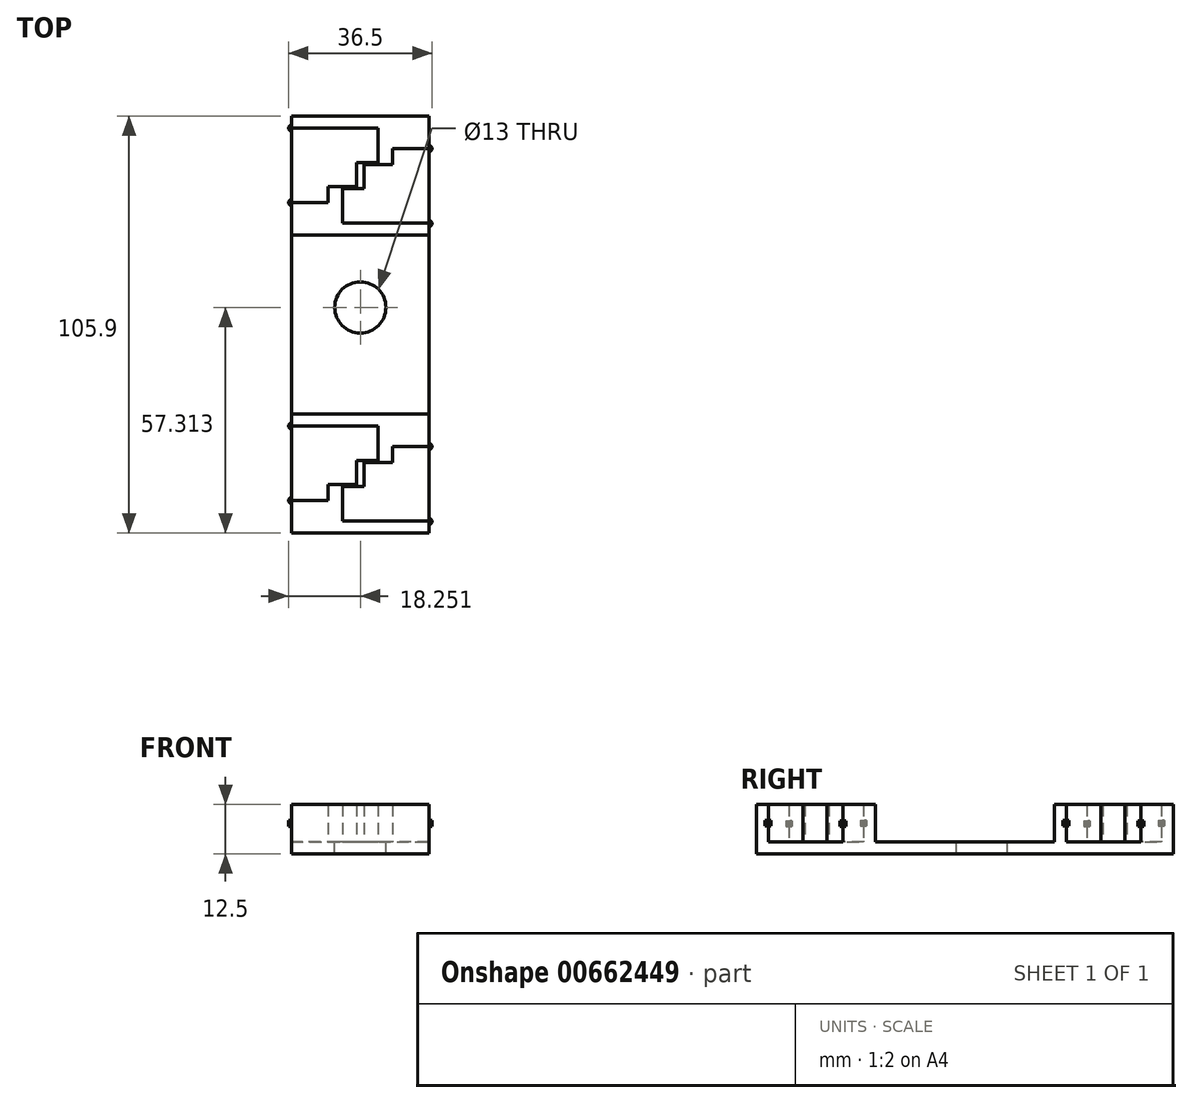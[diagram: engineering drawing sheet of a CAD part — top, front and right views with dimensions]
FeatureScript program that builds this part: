
annotation { "Feature Type Name" : "Feature", "Feature Type Description" : "" }
export const myFeature = defineFeature(function(context is Context, id is Id, definition is map)
    precondition{}
    {
        {
            var Q0;
            Q0=qCreatedBy(makeId("Top.planeOp"),FACE);
            var sketch = newSketch(context, id + "F0", { "sketchPlane" : qUnion([Q0])});
            skLineSegment(sketch, "E0.bottom", {"start": v(-9.64, 16.1) * mm, "end": v(7.86, 16.1) * mm});
            skLineSegment(sketch, "E0.left", {"start": v(-9.64, 16.1) * mm, "end": v(-9.64, -29.4) * mm});
            skLineSegment(sketch, "E1", {"start": v(7.86, 16.1) * mm, "end": v(25.36, 16.1) * mm});
            skCircle(sketch, "E2", {"center": v(7.86, -2.29) * mm, "radius": 6.5 * mm});
            skLineSegment(sketch, "E3.MirrorCS", {"start": v(-9.64, 43.3) * mm, "end": v(-6.47, 43.3) * mm});
            skLineSegment(sketch, "E4.MirrorCS", {"start": v(7.86, 27.9) * mm, "end": v(7.86, 34.5) * mm});
            skLineSegment(sketch, "E5.MirrorCS", {"start": v(-9.64, 24.3) * mm, "end": v(-0.34, 24.3) * mm});
            skLineSegment(sketch, "E6.MirrorCS", {"start": v(12.36, 35.3) * mm, "end": v(12.36, 43.3) * mm});
            skLineSegment(sketch, "E7.MirrorCS", {"start": v(-6.47, 43.3) * mm, "end": v(12.36, 43.3) * mm});
            skLineSegment(sketch, "E8.MirrorCS", {"start": v(-9.64, 24.3) * mm, "end": v(-9.64, 43.3) * mm});
            skPoint(sketch, "E9", {"position": v(7.86, 31.6) * mm});
            skLineSegment(sketch, "E10", {"start": v(-9.64, 16.1) * mm, "end": v(-9.64, 19.1) * mm});
            skLineSegment(sketch, "E11", {"start": v(-9.64, 19.1) * mm, "end": v(25.36, 19.1) * mm});
            skLineSegment(sketch, "E12", {"start": v(25.36, 19.1) * mm, "end": v(25.36, 19.1) * mm});
            skLineSegment(sketch, "E13", {"start": v(25.36, 19.1) * mm, "end": v(25.36, 16.1) * mm});
            skLineSegment(sketch, "E14.MirrorCS", {"start": v(25.36, 19.1) * mm, "end": v(22.2, 19.1) * mm});
            skLineSegment(sketch, "E15.MirrorCS", {"start": v(7.86, 34.5) * mm, "end": v(7.86, 27.9) * mm});
            skLineSegment(sketch, "E16.MirrorCS", {"start": v(25.36, 38.1) * mm, "end": v(16.06, 38.1) * mm});
            skLineSegment(sketch, "E17.MirrorCS", {"start": v(3.36, 27.1) * mm, "end": v(3.36, 19.1) * mm});
            skLineSegment(sketch, "E18.MirrorCS", {"start": v(22.2, 19.1) * mm, "end": v(3.36, 19.1) * mm});
            skLineSegment(sketch, "E19.MirrorCS", {"start": v(25.36, 38.1) * mm, "end": v(25.36, 19.1) * mm});
            skPoint(sketch, "E20", {"position": v(7.86, 30.8) * mm});
            skLineSegment(sketch, "E21", {"start": v(-9.64, 19.1) * mm, "end": v(-9.64, 24.3) * mm});
            skLineSegment(sketch, "E22", {"start": v(12.36, 43.3) * mm, "end": v(25.36, 43.3) * mm});
            skLineSegment(sketch, "E23", {"start": v(25.36, 43.3) * mm, "end": v(25.36, 38.1) * mm});
            skLineSegment(sketch, "E24", {"start": v(-9.64, 43.3) * mm, "end": v(-9.64, 46.3) * mm});
            skLineSegment(sketch, "E25", {"start": v(-9.64, 46.3) * mm, "end": v(25.36, 46.3) * mm});
            skLineSegment(sketch, "E26", {"start": v(25.36, 46.3) * mm, "end": v(25.36, 43.3) * mm});
            skLineSegment(sketch, "E27", {"start": v(25.36, -29.4) * mm, "end": v(-9.64, -29.4) * mm});
            skLineSegment(sketch, "E28", {"start": v(16.06, 38.1) * mm, "end": v(16.06, 34) * mm});
            skLineSegment(sketch, "E29", {"start": v(16.06, 34) * mm, "end": v(7.86, 34) * mm});
            skLineSegment(sketch, "E30", {"start": v(7.86, 34.5) * mm, "end": v(12.36, 34.5) * mm});
            skLineSegment(sketch, "E31", {"start": v(12.36, 34.5) * mm, "end": v(12.36, 35.3) * mm});
            skLineSegment(sketch, "E32", {"start": v(-0.34, 24.3) * mm, "end": v(-0.34, 28.4) * mm});
            skLineSegment(sketch, "E33", {"start": v(7.86, 27.9) * mm, "end": v(3.36, 27.9) * mm});
            skLineSegment(sketch, "E34", {"start": v(3.36, 27.9) * mm, "end": v(3.36, 27.1) * mm});
            skLineSegment(sketch, "E35", {"start": v(7.86, 34.5) * mm, "end": v(6.93, 34.5) * mm});
            skLineSegment(sketch, "E36", {"start": v(7.86, 27.9) * mm, "end": v(8.8, 27.9) * mm});
            skLineSegment(sketch, "E37", {"start": v(6.93, 34.5) * mm, "end": v(6.93, 28.4) * mm});
            skLineSegment(sketch, "E38", {"start": v(8.8, 27.9) * mm, "end": v(8.8, 34) * mm});
            skLineSegment(sketch, "E39", {"start": v(-0.34, 28.4) * mm, "end": v(7.86, 28.4) * mm});
            skPoint(sketch, "E40", {"position": v(-9.64, -6.65) * mm});
            skLineSegment(sketch, "E41", {"start": v(-37.32, -6.65) * mm, "end": v(44.88, -6.65) * mm, "construction": true});
            skLineSegment(sketch, "E42", {"start": v(25.36, 16.1) * mm, "end": v(25.36, -29.4) * mm});
            skLineSegment(sketch, "E43.MirrorCS", {"start": v(-9.64, -32.4) * mm, "end": v(-6.47, -32.4) * mm});
            skLineSegment(sketch, "E44.MirrorCS", {"start": v(7.86, -47.8) * mm, "end": v(7.86, -41.2) * mm});
            skLineSegment(sketch, "E45.MirrorCS", {"start": v(-9.64, -51.4) * mm, "end": v(-0.34, -51.4) * mm});
            skLineSegment(sketch, "E46.MirrorCS", {"start": v(12.36, -40.4) * mm, "end": v(12.36, -32.4) * mm});
            skLineSegment(sketch, "E47.MirrorCS", {"start": v(-6.47, -32.4) * mm, "end": v(12.36, -32.4) * mm});
            skLineSegment(sketch, "E48.MirrorCS", {"start": v(-9.64, -51.4) * mm, "end": v(-9.64, -32.4) * mm});
            skPoint(sketch, "E49", {"position": v(7.86, -44.1) * mm});
            skLineSegment(sketch, "E50", {"start": v(-9.64, -56.6) * mm, "end": v(25.36, -56.6) * mm});
            skLineSegment(sketch, "E51", {"start": v(21.02, 47.75) * mm, "end": v(21.02, 47.75) * mm});
            skLineSegment(sketch, "E52.MirrorCS", {"start": v(25.36, -56.6) * mm, "end": v(22.2, -56.6) * mm});
            skLineSegment(sketch, "E53.MirrorCS", {"start": v(7.86, -41.2) * mm, "end": v(7.86, -47.8) * mm});
            skLineSegment(sketch, "E54.MirrorCS", {"start": v(25.36, -37.6) * mm, "end": v(16.06, -37.6) * mm});
            skLineSegment(sketch, "E55.MirrorCS", {"start": v(3.36, -48.6) * mm, "end": v(3.36, -56.6) * mm});
            skLineSegment(sketch, "E56.MirrorCS", {"start": v(22.2, -56.6) * mm, "end": v(3.36, -56.6) * mm});
            skLineSegment(sketch, "E57.MirrorCS", {"start": v(25.36, -37.6) * mm, "end": v(25.36, -56.6) * mm});
            skPoint(sketch, "E58", {"position": v(7.86, -44.9) * mm});
            skLineSegment(sketch, "E59", {"start": v(-9.64, -56.6) * mm, "end": v(-9.64, -51.4) * mm});
            skLineSegment(sketch, "E60", {"start": v(12.36, -32.4) * mm, "end": v(25.36, -32.4) * mm});
            skLineSegment(sketch, "E61", {"start": v(25.36, -32.4) * mm, "end": v(25.36, -37.6) * mm});
            skLineSegment(sketch, "E62", {"start": v(-9.64, -32.4) * mm, "end": v(-9.64, -29.4) * mm});
            skLineSegment(sketch, "E63", {"start": v(-9.64, -29.4) * mm, "end": v(25.36, -29.4) * mm});
            skLineSegment(sketch, "E64", {"start": v(25.36, -29.4) * mm, "end": v(25.36, -32.4) * mm});
            skLineSegment(sketch, "E65", {"start": v(16.06, -37.6) * mm, "end": v(16.06, -41.7) * mm});
            skLineSegment(sketch, "E66", {"start": v(16.06, -41.7) * mm, "end": v(7.86, -41.7) * mm});
            skLineSegment(sketch, "E67", {"start": v(7.86, -41.2) * mm, "end": v(12.36, -41.2) * mm});
            skLineSegment(sketch, "E68", {"start": v(12.36, -41.2) * mm, "end": v(12.36, -40.4) * mm});
            skLineSegment(sketch, "E69", {"start": v(-0.34, -51.4) * mm, "end": v(-0.34, -47.3) * mm});
            skLineSegment(sketch, "E70", {"start": v(7.86, -47.8) * mm, "end": v(3.36, -47.8) * mm});
            skLineSegment(sketch, "E71", {"start": v(3.36, -47.8) * mm, "end": v(3.36, -48.6) * mm});
            skLineSegment(sketch, "E72", {"start": v(7.86, -41.2) * mm, "end": v(6.93, -41.2) * mm});
            skLineSegment(sketch, "E73", {"start": v(7.86, -47.8) * mm, "end": v(8.8, -47.8) * mm});
            skLineSegment(sketch, "E74", {"start": v(6.93, -41.2) * mm, "end": v(6.93, -47.3) * mm});
            skLineSegment(sketch, "E75", {"start": v(8.8, -47.8) * mm, "end": v(8.8, -41.7) * mm});
            skLineSegment(sketch, "E76", {"start": v(-0.34, -47.3) * mm, "end": v(7.86, -47.3) * mm});
            skLineSegment(sketch, "E77", {"start": v(-9.64, -59.6) * mm, "end": v(-9.64, -56.6) * mm});
            skLineSegment(sketch, "E78", {"start": v(-9.64, -59.6) * mm, "end": v(25.36, -59.6) * mm});
            skLineSegment(sketch, "E79", {"start": v(25.36, -59.6) * mm, "end": v(25.36, -56.6) * mm});
            skSolve(sketch);
        }
        {
            var Q0;
            Q0=makeQuery(id+"F0.imprint","IMPRINT",FACE,{"disambiguationData":[TD([[makeQuery(id+"F0.imprint","IMPRINT",EDGE,{"derivedFrom":sQuery(id+"F0.wireOp",EDGE,"E0.bottom")}),-1.0]])]});
            var Q1;
            Q1=makeQuery(id+"F0.imprint","IMPRINT",FACE,{"disambiguationData":[TD([[makeQuery(id+"F0.imprint","IMPRINT",EDGE,{"derivedFrom":sQuery(id+"F0.wireOp",EDGE,"E27")}),1.0]])]});
            var Q2;
            Q2=makeQuery(id+"F0.imprint","IMPRINT",FACE,{"disambiguationData":[TD([[makeQuery(id+"F0.imprint","IMPRINT",EDGE,{"derivedFrom":sQuery(id+"F0.wireOp",EDGE,"82a180c3-1ea1-40ab-986d-dace1a723f1b2.MirrorCS")}),1.0]])]});
            var Q3;
            Q3=makeQuery(id+"F0.imprint","IMPRINT",FACE,{"disambiguationData":[TD([[makeQuery(id+"F0.imprint","IMPRINT",EDGE,{"derivedFrom":sQuery(id+"F0.wireOp",EDGE,"82a180c3-1ea1-40ab-986d-dace1a723f1b1.MirrorCS")}),1.0]])]});
            var Q4;
            Q4=makeQuery(id+"F0.imprint","IMPRINT",FACE,{"disambiguationData":[TD([[makeQuery(id+"F0.imprint","IMPRINT",EDGE,{"derivedFrom":sQuery(id+"F0.wireOp",EDGE,"82a180c3-1ea1-40ab-986d-dace1a723f1b4.MirrorCS")}),1.0]])]});
            var Q5;
            {var subQ2=sQuery(id+"F0.wireOp",EDGE,"82a180c3-1ea1-40ab-986d-dace1a723f1b0.MirrorCS");Q5=makeQuery(id+"F0.imprint","IMPRINT",FACE,{"disambiguationData":[TD([[makeQuery(id+"F0.imprint","IMPRINT",EDGE,{"derivedFrom":subQ2}),-1.0]])]});}
            var Q6;
            {var subQ5=sQuery(id+"F0.wireOp",EDGE,"82a180c3-1ea1-40ab-986d-dace1a723f1b1.MirrorCS");Q6=makeQuery(id+"F0.imprint","IMPRINT",FACE,{"disambiguationData":[TD([[makeQuery(id+"F0.imprint","IMPRINT",EDGE,{"derivedFrom":subQ5}),-1.0]])]});}
            var Q7;
            Q7=makeQuery(id+"F0.imprint","IMPRINT",FACE,{"disambiguationData":[TD([[makeQuery(id+"F0.imprint","IMPRINT",EDGE,{"derivedFrom":sQuery(id+"F0.wireOp",EDGE,"82a180c3-1ea1-40ab-986d-dace1a723f1b0.MirrorCS")}),1.0]])]});
            var Q8;
            Q8=makeQuery(id+"F0.imprint","IMPRINT",FACE,{"disambiguationData":[TD([[makeQuery(id+"F0.imprint","IMPRINT",EDGE,{"derivedFrom":sQuery(id+"F0.wireOp",EDGE,"82a180c3-1ea1-40ab-986d-dace1a723f1b16.MirrorCS")}),-1.0]])]});
            var Q9;
            Q9=makeQuery(id+"F0.imprint","IMPRINT",FACE,{"disambiguationData":[TD([[makeQuery(id+"F0.imprint","IMPRINT",EDGE,{"derivedFrom":sQuery(id+"F0.wireOp",EDGE,"E3.MirrorCS")}),1.0]])]});
            var Q10;
            Q10=makeQuery(id+"F0.imprint","IMPRINT",FACE,{"disambiguationData":[TD([[makeQuery(id+"F0.imprint","IMPRINT",EDGE,{"derivedFrom":sQuery(id+"F0.wireOp",EDGE,"E6.MirrorCS")}),-1.0]])]});
            var Q11;
            Q11=makeQuery(id+"F0.imprint","IMPRINT",FACE,{"disambiguationData":[TD([[makeQuery(id+"F0.imprint","IMPRINT",EDGE,{"derivedFrom":sQuery(id+"F0.wireOp",EDGE,"E3.MirrorCS")}),-1.0]])]});
            var Q12;
            Q12=makeQuery(id+"F0.imprint","IMPRINT",FACE,{"disambiguationData":[TD([[makeQuery(id+"F0.imprint","IMPRINT",EDGE,{"derivedFrom":sQuery(id+"F0.wireOp",EDGE,"E16.MirrorCS")}),1.0]])]});
            var Q13;
            Q13=makeQuery(id+"F0.imprint","IMPRINT",FACE,{"disambiguationData":[TD([[makeQuery(id+"F0.imprint","IMPRINT",EDGE,{"derivedFrom":sQuery(id+"F0.wireOp",EDGE,"E0.bottom")}),1.0]])]});
            var Q14;
            Q14=makeQuery(id+"F0.imprint","IMPRINT",FACE,{"disambiguationData":[TD([[makeQuery(id+"F0.imprint","IMPRINT",EDGE,{"derivedFrom":sQuery(id+"F0.wireOp",EDGE,"E5.MirrorCS")}),-1.0]])]});
            var Q15;
            {var subQ1=sQuery(id+"F0.wireOp",EDGE,"E35");Q15=makeQuery(id+"F0.imprint","IMPRINT",FACE,{"disambiguationData":[TD([[makeQuery(id+"F0.imprint","IMPRINT",EDGE,{"derivedFrom":subQ1}),1.0]])]});}
            var Q16;
            {var subQ4=sQuery(id+"F0.wireOp",EDGE,"E36");Q16=makeQuery(id+"F0.imprint","IMPRINT",FACE,{"disambiguationData":[TD([[makeQuery(id+"F0.imprint","IMPRINT",EDGE,{"derivedFrom":subQ4}),1.0]])]});}
            var Q17;
            Q17=makeQuery(id+"F0.imprint","IMPRINT",FACE,{"disambiguationData":[TD([[makeQuery(id+"F0.imprint","IMPRINT",EDGE,{"derivedFrom":sQuery(id+"F0.wireOp",EDGE,"E43.MirrorCS")}),-1.0]])]});
            var Q18;
            Q18=makeQuery(id+"F0.imprint","IMPRINT",FACE,{"disambiguationData":[TD([[makeQuery(id+"F0.imprint","IMPRINT",EDGE,{"derivedFrom":sQuery(id+"F0.wireOp",EDGE,"E54.MirrorCS")}),1.0]])]});
            var Q19;
            Q19=makeQuery(id+"F0.imprint","IMPRINT",FACE,{"disambiguationData":[TD([[makeQuery(id+"F0.imprint","IMPRINT",EDGE,{"derivedFrom":sQuery(id+"F0.wireOp",EDGE,"E46.MirrorCS")}),-1.0]])]});
            var Q20;
            Q20=makeQuery(id+"F0.imprint","IMPRINT",FACE,{"disambiguationData":[TD([[makeQuery(id+"F0.imprint","IMPRINT",EDGE,{"derivedFrom":sQuery(id+"F0.wireOp",EDGE,"E27")}),1.0]])]});
            var Q21;
            Q21=makeQuery(id+"F0.imprint","IMPRINT",FACE,{"disambiguationData":[TD([[makeQuery(id+"F0.imprint","IMPRINT",EDGE,{"derivedFrom":sQuery(id+"F0.wireOp",EDGE,"E45.MirrorCS")}),-1.0]])]});
            var Q22;
            {var subQ0=sQuery(id+"F0.wireOp",EDGE,"E73");Q22=makeQuery(id+"F0.imprint","IMPRINT",FACE,{"disambiguationData":[TD([[makeQuery(id+"F0.imprint","IMPRINT",EDGE,{"derivedFrom":subQ0}),1.0]])]});}
            var Q23;
            {var subQ1=sQuery(id+"F0.wireOp",EDGE,"E72");Q23=makeQuery(id+"F0.imprint","IMPRINT",FACE,{"disambiguationData":[TD([[makeQuery(id+"F0.imprint","IMPRINT",EDGE,{"derivedFrom":subQ1}),1.0]])]});}
            var Q24;
            {var subQ4=sQuery(id+"F0.wireOp",EDGE,"E77");Q24=makeQuery(id+"F0.imprint","IMPRINT",FACE,{"disambiguationData":[TD([[makeQuery(id+"F0.imprint","IMPRINT",EDGE,{"derivedFrom":subQ4}),-1.0]])]});}
            extrude(context, id + "F1", {"entities" : qUnion([Q0, Q1, Q2, Q3, Q4, Q5, Q6, Q7, Q8, Q9, Q10, Q11, Q12, Q13, Q14, Q15, Q16, Q17, Q18, Q19, Q20, Q21, Q22, Q23, Q24]), "oppositeDirection" : true, "depth" : 3 * mm, "offsetDistance" : 25 * mm});
        }
        {
            var Q0;
            Q0=makeQuery(id+"F0.imprint","IMPRINT",FACE,{"disambiguationData":[TD([[makeQuery(id+"F0.imprint","IMPRINT",EDGE,{"derivedFrom":sQuery(id+"F0.wireOp",EDGE,"E0.bottom")}),1.0]])]});
            var Q1;
            Q1=makeQuery(id+"F0.imprint","IMPRINT",FACE,{"disambiguationData":[TD([[makeQuery(id+"F0.imprint","IMPRINT",EDGE,{"derivedFrom":sQuery(id+"F0.wireOp",EDGE,"E5.MirrorCS")}),-1.0]])]});
            var Q2;
            Q2=makeQuery(id+"F0.imprint","IMPRINT",FACE,{"disambiguationData":[TD([[makeQuery(id+"F0.imprint","IMPRINT",EDGE,{"derivedFrom":sQuery(id+"F0.wireOp",EDGE,"E3.MirrorCS")}),1.0]])]});
            var Q3;
            Q3=makeQuery(id+"F0.imprint","IMPRINT",FACE,{"disambiguationData":[TD([[makeQuery(id+"F0.imprint","IMPRINT",EDGE,{"derivedFrom":sQuery(id+"F0.wireOp",EDGE,"E6.MirrorCS")}),-1.0]])]});
            var Q4;
            {var subQ1=sQuery(id+"F0.wireOp",EDGE,"E35");Q4=makeQuery(id+"F0.imprint","IMPRINT",FACE,{"disambiguationData":[TD([[makeQuery(id+"F0.imprint","IMPRINT",EDGE,{"derivedFrom":subQ1}),1.0]])]});}
            var Q5;
            {var subQ4=sQuery(id+"F0.wireOp",EDGE,"E36");Q5=makeQuery(id+"F0.imprint","IMPRINT",FACE,{"disambiguationData":[TD([[makeQuery(id+"F0.imprint","IMPRINT",EDGE,{"derivedFrom":subQ4}),1.0]])]});}
            var Q6;
            Q6=makeQuery(id+"F0.imprint","IMPRINT",FACE,{"disambiguationData":[TD([[makeQuery(id+"F0.imprint","IMPRINT",EDGE,{"derivedFrom":sQuery(id+"F0.wireOp",EDGE,"E27")}),1.0]])]});
            var Q7;
            Q7=makeQuery(id+"F0.imprint","IMPRINT",FACE,{"disambiguationData":[TD([[makeQuery(id+"F0.imprint","IMPRINT",EDGE,{"derivedFrom":sQuery(id+"F0.wireOp",EDGE,"82a180c3-1ea1-40ab-986d-dace1a723f1b2.MirrorCS")}),1.0]])]});
            var Q8;
            {var subQ5=sQuery(id+"F0.wireOp",EDGE,"82a180c3-1ea1-40ab-986d-dace1a723f1b1.MirrorCS");Q8=makeQuery(id+"F0.imprint","IMPRINT",FACE,{"disambiguationData":[TD([[makeQuery(id+"F0.imprint","IMPRINT",EDGE,{"derivedFrom":subQ5}),-1.0]])]});}
            var Q9;
            {var subQ2=sQuery(id+"F0.wireOp",EDGE,"82a180c3-1ea1-40ab-986d-dace1a723f1b0.MirrorCS");Q9=makeQuery(id+"F0.imprint","IMPRINT",FACE,{"disambiguationData":[TD([[makeQuery(id+"F0.imprint","IMPRINT",EDGE,{"derivedFrom":subQ2}),-1.0]])]});}
            var Q10;
            Q10=makeQuery(id+"F0.imprint","IMPRINT",FACE,{"disambiguationData":[TD([[makeQuery(id+"F0.imprint","IMPRINT",EDGE,{"derivedFrom":sQuery(id+"F0.wireOp",EDGE,"82a180c3-1ea1-40ab-986d-dace1a723f1b4.MirrorCS")}),1.0]])]});
            var Q11;
            Q11=makeQuery(id+"F0.imprint","IMPRINT",FACE,{"disambiguationData":[TD([[makeQuery(id+"F0.imprint","IMPRINT",EDGE,{"derivedFrom":sQuery(id+"F0.wireOp",EDGE,"82a180c3-1ea1-40ab-986d-dace1a723f1b16.MirrorCS")}),-1.0]])]});
            var Q12;
            Q12=makeQuery(id+"F0.imprint","IMPRINT",FACE,{"disambiguationData":[TD([[makeQuery(id+"F0.imprint","IMPRINT",EDGE,{"derivedFrom":sQuery(id+"F0.wireOp",EDGE,"E46.MirrorCS")}),-1.0]])]});
            var Q13;
            Q13=makeQuery(id+"F0.imprint","IMPRINT",FACE,{"disambiguationData":[TD([[makeQuery(id+"F0.imprint","IMPRINT",EDGE,{"derivedFrom":sQuery(id+"F0.wireOp",EDGE,"E27")}),1.0]])]});
            var Q14;
            Q14=makeQuery(id+"F0.imprint","IMPRINT",FACE,{"disambiguationData":[TD([[makeQuery(id+"F0.imprint","IMPRINT",EDGE,{"derivedFrom":sQuery(id+"F0.wireOp",EDGE,"E45.MirrorCS")}),-1.0]])]});
            var Q15;
            {var subQ0=sQuery(id+"F0.wireOp",EDGE,"E73");Q15=makeQuery(id+"F0.imprint","IMPRINT",FACE,{"disambiguationData":[TD([[makeQuery(id+"F0.imprint","IMPRINT",EDGE,{"derivedFrom":subQ0}),1.0]])]});}
            var Q16;
            {var subQ1=sQuery(id+"F0.wireOp",EDGE,"E72");Q16=makeQuery(id+"F0.imprint","IMPRINT",FACE,{"disambiguationData":[TD([[makeQuery(id+"F0.imprint","IMPRINT",EDGE,{"derivedFrom":subQ1}),1.0]])]});}
            var Q17;
            {var subQ4=sQuery(id+"F0.wireOp",EDGE,"E77");Q17=makeQuery(id+"F0.imprint","IMPRINT",FACE,{"disambiguationData":[TD([[makeQuery(id+"F0.imprint","IMPRINT",EDGE,{"derivedFrom":subQ4}),-1.0]])]});}
            extrude(context, id + "F2", {"entities" : qUnion([Q0, Q1, Q2, Q3, Q4, Q5, Q6, Q7, Q8, Q9, Q10, Q11, Q12, Q13, Q14, Q15, Q16, Q17]), "operationType" : NewBodyOperationType.ADD, "depth" : 9.5 * mm, "offsetDistance" : 25 * mm});
        }
        {
            var Q0;
            {var subQ0=sQuery(id+"F0.wireOp",EDGE,"E79");var subQ1=sQuery(id+"F0.wireOp",EDGE,"E64");var subQ2=sQuery(id+"F0.wireOp",EDGE,"E61");var subQ3=sQuery(id+"F0.wireOp",EDGE,"E26");var subQ4=sQuery(id+"F0.wireOp",EDGE,"E23");var subQ5=sQuery(id+"F0.wireOp",EDGE,"E13");Q0=makeQuery(id+"F2.boolean.opBoolean","MERGE",FACE,{"derivedFrom":[makeQuery(id+"F1.opExtrude","SWEPT_FACE",FACE,{"disambiguationData":[OSD([subQ5,sQuery(id+"F0.wireOp",EDGE,"E19.MirrorCS"),subQ4,subQ3,sQuery(id+"F0.wireOp",EDGE,"E42"),sQuery(id+"F0.wireOp",EDGE,"E57.MirrorCS"),subQ2,subQ1,subQ0])]}),makeQuery(id+"F2.opExtrude","SWEPT_FACE",FACE,{"disambiguationData":[OSD([subQ5])]}),makeQuery(id+"F2.opExtrude","SWEPT_FACE",FACE,{"disambiguationData":[OSD([subQ4,subQ3])]}),makeQuery(id+"F2.opExtrude","SWEPT_FACE",FACE,{"disambiguationData":[OSD([subQ2,subQ1])]}),makeQuery(id+"F2.opExtrude","SWEPT_FACE",FACE,{"disambiguationData":[OSD([subQ0])]})]});}
            var sketch = newSketch(context, id + "F3", { "sketchPlane" : qUnion([Q0])});
            skPoint(sketch, "E80.0", {"position": v(-37.6, 4.75) * mm});
            skLineSegment(sketch, "E81.bottom", {"start": v(-36.84, 5.4) * mm, "end": v(-38.34, 5.4) * mm});
            skLineSegment(sketch, "E81.top", {"start": v(-36.84, 4) * mm, "end": v(-38.34, 4) * mm});
            skLineSegment(sketch, "E81.left", {"start": v(-36.84, 5.4) * mm, "end": v(-36.84, 4) * mm});
            skLineSegment(sketch, "E81.right", {"start": v(-38.34, 5.4) * mm, "end": v(-38.34, 4) * mm});
            skPoint(sketch, "E82.5", {"position": v(-56.6, 4.75) * mm});
            skPoint(sketch, "E83.0", {"position": v(-56.63, 4.76) * mm});
            skLineSegment(sketch, "E84.bottom", {"start": v(-55.89, 5.41) * mm, "end": v(-57.39, 5.41) * mm});
            skLineSegment(sketch, "E84.top", {"start": v(-55.89, 4.02) * mm, "end": v(-57.39, 4.02) * mm});
            skLineSegment(sketch, "E84.left", {"start": v(-55.89, 5.41) * mm, "end": v(-55.89, 4.02) * mm});
            skLineSegment(sketch, "E84.right", {"start": v(-57.39, 5.41) * mm, "end": v(-57.39, 4.02) * mm});
            skPoint(sketch, "E85.0", {"position": v(19.1, 4.75) * mm});
            skPoint(sketch, "E85.1", {"position": v(38.1, 4.75) * mm});
            skLineSegment(sketch, "E86.bottom", {"start": v(38.76, 5.4) * mm, "end": v(37.26, 5.4) * mm});
            skLineSegment(sketch, "E86.top", {"start": v(38.76, 4) * mm, "end": v(37.26, 4) * mm});
            skLineSegment(sketch, "E86.left", {"start": v(38.76, 5.4) * mm, "end": v(38.76, 4) * mm});
            skLineSegment(sketch, "E86.right", {"start": v(37.26, 5.4) * mm, "end": v(37.26, 4) * mm});
            skPoint(sketch, "E87.0", {"position": v(19.07, 4.76) * mm});
            skLineSegment(sketch, "E88.bottom", {"start": v(19.8, 5.41) * mm, "end": v(18.3, 5.41) * mm});
            skLineSegment(sketch, "E88.top", {"start": v(19.8, 4.02) * mm, "end": v(18.3, 4.02) * mm});
            skLineSegment(sketch, "E88.left", {"start": v(19.8, 5.41) * mm, "end": v(19.8, 4.02) * mm});
            skLineSegment(sketch, "E88.right", {"start": v(18.3, 5.41) * mm, "end": v(18.3, 4.02) * mm});
            skSolve(sketch);
        }
        {
            var Q0;
            {var subQ0=sQuery(id+"F3.wireOp",EDGE,"E88.left");Q0=makeQuery(id+"F3.imprint","IMPRINT",FACE,{"disambiguationData":[TD([[makeQuery(id+"F3.imprint","IMPRINT",EDGE,{"derivedFrom":subQ0}),-1.0]])]});}
            var Q1;
            {var subQ0=sQuery(id+"F3.wireOp",EDGE,"E88.right");Q1=makeQuery(id+"F3.imprint","IMPRINT",FACE,{"disambiguationData":[TD([[makeQuery(id+"F3.imprint","IMPRINT",EDGE,{"derivedFrom":subQ0}),1.0]])]});}
            var Q2;
            {var subQ0=sQuery(id+"F3.wireOp",EDGE,"E86.right");Q2=makeQuery(id+"F3.imprint","IMPRINT",FACE,{"disambiguationData":[TD([[makeQuery(id+"F3.imprint","IMPRINT",EDGE,{"derivedFrom":subQ0}),1.0]])]});}
            var Q3;
            {var subQ0=sQuery(id+"F3.wireOp",EDGE,"E86.left");Q3=makeQuery(id+"F3.imprint","IMPRINT",FACE,{"disambiguationData":[TD([[makeQuery(id+"F3.imprint","IMPRINT",EDGE,{"derivedFrom":subQ0}),-1.0]])]});}
            var Q4;
            {var subQ0=sQuery(id+"F3.wireOp",EDGE,"E81.left");Q4=makeQuery(id+"F3.imprint","IMPRINT",FACE,{"disambiguationData":[TD([[makeQuery(id+"F3.imprint","IMPRINT",EDGE,{"derivedFrom":subQ0}),-1.0]])]});}
            var Q5;
            {var subQ0=sQuery(id+"F3.wireOp",EDGE,"E81.right");Q5=makeQuery(id+"F3.imprint","IMPRINT",FACE,{"disambiguationData":[TD([[makeQuery(id+"F3.imprint","IMPRINT",EDGE,{"derivedFrom":subQ0}),1.0]])]});}
            var Q6;
            {var subQ0=sQuery(id+"F3.wireOp",EDGE,"E84.left");Q6=makeQuery(id+"F3.imprint","IMPRINT",FACE,{"disambiguationData":[TD([[makeQuery(id+"F3.imprint","IMPRINT",EDGE,{"derivedFrom":subQ0}),-1.0]])]});}
            var Q7;
            {var subQ0=sQuery(id+"F3.wireOp",EDGE,"E84.right");Q7=makeQuery(id+"F3.imprint","IMPRINT",FACE,{"disambiguationData":[TD([[makeQuery(id+"F3.imprint","IMPRINT",EDGE,{"derivedFrom":subQ0}),1.0]])]});}
            extrude(context, id + "F4", {"entities" : qUnion([Q0, Q1, Q2, Q3, Q4, Q5, Q6, Q7]), "operationType" : NewBodyOperationType.ADD, "depth" : .75 * mm, "offsetDistance" : 25 * mm});
        }
        {
            var Q0;
            {var subQ0=sQuery(id+"F0.wireOp",EDGE,"E62");var subQ1=sQuery(id+"F0.wireOp",EDGE,"E77");var subQ2=sQuery(id+"F0.wireOp",EDGE,"E59");var subQ3=sQuery(id+"F0.wireOp",EDGE,"E24");var subQ4=sQuery(id+"F0.wireOp",EDGE,"E21");var subQ5=sQuery(id+"F0.wireOp",EDGE,"E10");Q0=makeQuery(id+"F2.boolean.opBoolean","MERGE",FACE,{"derivedFrom":[makeQuery(id+"F1.opExtrude","SWEPT_FACE",FACE,{"disambiguationData":[OSD([sQuery(id+"F0.wireOp",EDGE,"E0.left"),sQuery(id+"F0.wireOp",EDGE,"E8.MirrorCS"),subQ5,subQ4,subQ3,sQuery(id+"F0.wireOp",EDGE,"E48.MirrorCS"),subQ2,subQ0,subQ1])]}),makeQuery(id+"F2.opExtrude","SWEPT_FACE",FACE,{"disambiguationData":[OSD([subQ5,subQ4])]}),makeQuery(id+"F2.opExtrude","SWEPT_FACE",FACE,{"disambiguationData":[OSD([subQ3])]}),makeQuery(id+"F2.opExtrude","SWEPT_FACE",FACE,{"disambiguationData":[OSD([subQ2,subQ1])]}),makeQuery(id+"F2.opExtrude","SWEPT_FACE",FACE,{"disambiguationData":[OSD([subQ0])]})]});}
            var sketch = newSketch(context, id + "F5", { "sketchPlane" : qUnion([Q0])});
            skPoint(sketch, "E89.0", {"position": v(-43.3, 4.75) * mm});
            skPoint(sketch, "E89.1", {"position": v(-24.3, 4.75) * mm});
            skPoint(sketch, "E89.2", {"position": v(32.4, 4.75) * mm});
            skPoint(sketch, "E89.3", {"position": v(51.4, 4.75) * mm});
            skLineSegment(sketch, "E90.bottom", {"start": v(-23.6, 5.4) * mm, "end": v(-25.1, 5.4) * mm});
            skLineSegment(sketch, "E90.top", {"start": v(-23.6, 4) * mm, "end": v(-25.1, 4) * mm});
            skLineSegment(sketch, "E90.left", {"start": v(-23.6, 5.4) * mm, "end": v(-23.6, 4) * mm});
            skLineSegment(sketch, "E90.right", {"start": v(-25.1, 5.4) * mm, "end": v(-25.1, 4) * mm});
            skPoint(sketch, "E91.0", {"position": v(-43.33, 4.76) * mm});
            skLineSegment(sketch, "E92.bottom", {"start": v(-42.55, 5.41) * mm, "end": v(-44.05, 5.41) * mm});
            skLineSegment(sketch, "E92.top", {"start": v(-42.55, 4.02) * mm, "end": v(-44.05, 4.02) * mm});
            skLineSegment(sketch, "E92.left", {"start": v(-42.55, 5.41) * mm, "end": v(-42.55, 4.02) * mm});
            skLineSegment(sketch, "E92.right", {"start": v(-44.05, 5.41) * mm, "end": v(-44.05, 4.02) * mm});
            skLineSegment(sketch, "E93.bottom", {"start": v(52.13, 5.4) * mm, "end": v(50.63, 5.4) * mm});
            skLineSegment(sketch, "E93.top", {"start": v(52.13, 4) * mm, "end": v(50.63, 4) * mm});
            skLineSegment(sketch, "E93.left", {"start": v(52.13, 5.4) * mm, "end": v(52.13, 4) * mm});
            skLineSegment(sketch, "E93.right", {"start": v(50.63, 5.4) * mm, "end": v(50.63, 4) * mm});
            skPoint(sketch, "E94.0", {"position": v(32.37, 4.76) * mm});
            skLineSegment(sketch, "E95.bottom", {"start": v(33.17, 5.41) * mm, "end": v(31.67, 5.41) * mm});
            skLineSegment(sketch, "E95.top", {"start": v(33.17, 4.02) * mm, "end": v(31.67, 4.02) * mm});
            skLineSegment(sketch, "E95.left", {"start": v(33.17, 5.41) * mm, "end": v(33.17, 4.02) * mm});
            skLineSegment(sketch, "E95.right", {"start": v(31.67, 5.41) * mm, "end": v(31.67, 4.02) * mm});
            skSolve(sketch);
        }
        {
            var Q0;
            {var subQ0=sQuery(id+"F5.wireOp",EDGE,"E93.left");Q0=makeQuery(id+"F5.imprint","IMPRINT",FACE,{"disambiguationData":[TD([[makeQuery(id+"F5.imprint","IMPRINT",EDGE,{"derivedFrom":subQ0}),-1.0]])]});}
            var Q1;
            {var subQ0=sQuery(id+"F5.wireOp",EDGE,"E93.right");Q1=makeQuery(id+"F5.imprint","IMPRINT",FACE,{"disambiguationData":[TD([[makeQuery(id+"F5.imprint","IMPRINT",EDGE,{"derivedFrom":subQ0}),1.0]])]});}
            var Q2;
            {var subQ0=sQuery(id+"F5.wireOp",EDGE,"E95.left");Q2=makeQuery(id+"F5.imprint","IMPRINT",FACE,{"disambiguationData":[TD([[makeQuery(id+"F5.imprint","IMPRINT",EDGE,{"derivedFrom":subQ0}),-1.0]])]});}
            var Q3;
            {var subQ0=sQuery(id+"F5.wireOp",EDGE,"E95.right");Q3=makeQuery(id+"F5.imprint","IMPRINT",FACE,{"disambiguationData":[TD([[makeQuery(id+"F5.imprint","IMPRINT",EDGE,{"derivedFrom":subQ0}),1.0]])]});}
            var Q4;
            {var subQ0=sQuery(id+"F5.wireOp",EDGE,"E90.left");Q4=makeQuery(id+"F5.imprint","IMPRINT",FACE,{"disambiguationData":[TD([[makeQuery(id+"F5.imprint","IMPRINT",EDGE,{"derivedFrom":subQ0}),-1.0]])]});}
            var Q5;
            {var subQ0=sQuery(id+"F5.wireOp",EDGE,"E90.right");Q5=makeQuery(id+"F5.imprint","IMPRINT",FACE,{"disambiguationData":[TD([[makeQuery(id+"F5.imprint","IMPRINT",EDGE,{"derivedFrom":subQ0}),1.0]])]});}
            var Q6;
            {var subQ0=sQuery(id+"F5.wireOp",EDGE,"E92.left");Q6=makeQuery(id+"F5.imprint","IMPRINT",FACE,{"disambiguationData":[TD([[makeQuery(id+"F5.imprint","IMPRINT",EDGE,{"derivedFrom":subQ0}),-1.0]])]});}
            var Q7;
            {var subQ0=sQuery(id+"F5.wireOp",EDGE,"E92.right");Q7=makeQuery(id+"F5.imprint","IMPRINT",FACE,{"disambiguationData":[TD([[makeQuery(id+"F5.imprint","IMPRINT",EDGE,{"derivedFrom":subQ0}),1.0]])]});}
            extrude(context, id + "F6", {"entities" : qUnion([Q0, Q1, Q2, Q3, Q4, Q5, Q6, Q7]), "operationType" : NewBodyOperationType.ADD, "depth" : .75 * mm, "offsetDistance" : 25 * mm});
        }
        {
            var Q0;
            Q0=makeQuery(id+"F4.opExtrude","CAP_EDGE",EDGE,{"disambiguationData":[OSD([sQuery(id+"F3.wireOp",EDGE,"E86.left")])],"isStart":false});
            var Q1;
            Q1=makeQuery(id+"F4.opExtrude","CAP_EDGE",EDGE,{"disambiguationData":[OSD([sQuery(id+"F3.wireOp",EDGE,"E86.right")])],"isStart":false});
            var Q2;
            Q2=makeQuery(id+"F4.opExtrude","CAP_EDGE",EDGE,{"disambiguationData":[OSD([sQuery(id+"F3.wireOp",EDGE,"E88.left")])],"isStart":false});
            var Q3;
            Q3=makeQuery(id+"F4.opExtrude","CAP_EDGE",EDGE,{"disambiguationData":[OSD([sQuery(id+"F3.wireOp",EDGE,"E88.right")])],"isStart":false});
            var Q4;
            Q4=makeQuery(id+"F4.opExtrude","CAP_EDGE",EDGE,{"disambiguationData":[OSD([sQuery(id+"F3.wireOp",EDGE,"E81.left")])],"isStart":false});
            var Q5;
            Q5=makeQuery(id+"F4.opExtrude","CAP_EDGE",EDGE,{"disambiguationData":[OSD([sQuery(id+"F3.wireOp",EDGE,"E81.right")])],"isStart":false});
            var Q6;
            Q6=makeQuery(id+"F4.opExtrude","CAP_EDGE",EDGE,{"disambiguationData":[OSD([sQuery(id+"F3.wireOp",EDGE,"E84.left")])],"isStart":false});
            var Q7;
            Q7=makeQuery(id+"F4.opExtrude","CAP_EDGE",EDGE,{"disambiguationData":[OSD([sQuery(id+"F3.wireOp",EDGE,"E84.right")])],"isStart":false});
            var Q8;
            Q8=makeQuery(id+"F6.opExtrude","CAP_EDGE",EDGE,{"disambiguationData":[OSD([sQuery(id+"F5.wireOp",EDGE,"E93.left")])],"isStart":false});
            var Q9;
            Q9=makeQuery(id+"F6.opExtrude","CAP_EDGE",EDGE,{"disambiguationData":[OSD([sQuery(id+"F5.wireOp",EDGE,"E93.right")])],"isStart":false});
            var Q10;
            Q10=makeQuery(id+"F6.opExtrude","CAP_EDGE",EDGE,{"disambiguationData":[OSD([sQuery(id+"F5.wireOp",EDGE,"E95.left")])],"isStart":false});
            var Q11;
            Q11=makeQuery(id+"F6.opExtrude","CAP_EDGE",EDGE,{"disambiguationData":[OSD([sQuery(id+"F5.wireOp",EDGE,"E95.right")])],"isStart":false});
            var Q12;
            Q12=makeQuery(id+"F6.opExtrude","CAP_EDGE",EDGE,{"disambiguationData":[OSD([sQuery(id+"F5.wireOp",EDGE,"E90.left")])],"isStart":false});
            var Q13;
            Q13=makeQuery(id+"F6.opExtrude","CAP_EDGE",EDGE,{"disambiguationData":[OSD([sQuery(id+"F5.wireOp",EDGE,"E90.right")])],"isStart":false});
            var Q14;
            Q14=makeQuery(id+"F6.opExtrude","CAP_EDGE",EDGE,{"disambiguationData":[OSD([sQuery(id+"F5.wireOp",EDGE,"E92.left")])],"isStart":false});
            var Q15;
            Q15=makeQuery(id+"F6.opExtrude","CAP_EDGE",EDGE,{"disambiguationData":[OSD([sQuery(id+"F5.wireOp",EDGE,"E92.right")])],"isStart":false});
            chamfer(context, id + "F7", {"entities" : qUnion([Q0, Q1, Q2, Q3, Q4, Q5, Q6, Q7, Q8, Q9, Q10, Q11, Q12, Q13, Q14, Q15]), "width" : .5 * mm, "tangentPropagation" : true});
        }
    });
